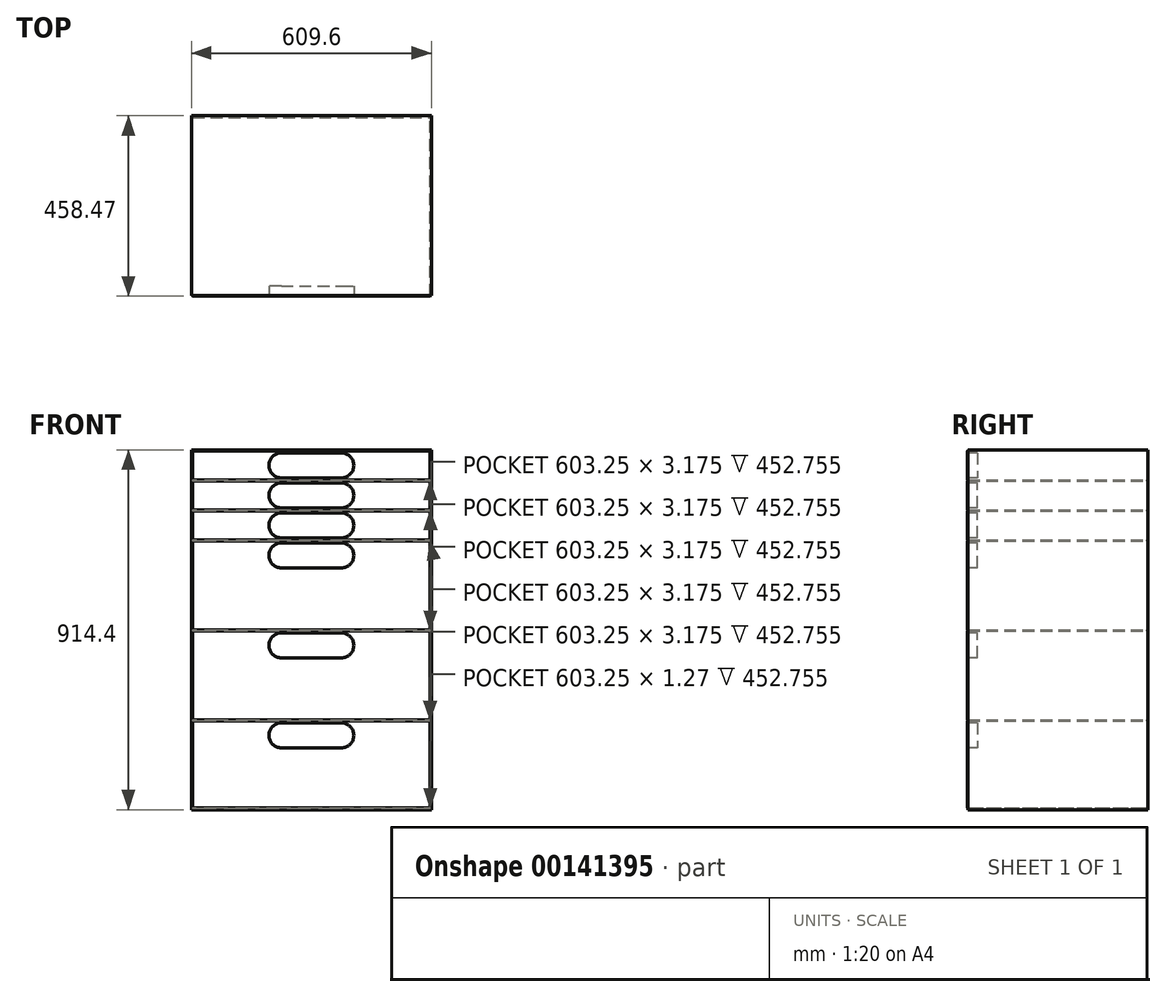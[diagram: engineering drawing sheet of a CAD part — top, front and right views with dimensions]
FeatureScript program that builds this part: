
annotation { "Feature Type Name" : "Feature", "Feature Type Description" : "" }
export const myFeature = defineFeature(function(context is Context, id is Id, definition is map)
    precondition{}
    {
        {
            var Q0;
            Q0=qCreatedBy(makeId("Top.planeOp"),FACE);
            var sketch = newSketch(context, id + "F0", { "sketchPlane" : qUnion([Q0])});
            skLineSegment(sketch, "E0.bottom", {"start": v(-304.8, 228.6) * mm, "end": v(304.8, 228.6) * mm});
            skLineSegment(sketch, "E0.top", {"start": v(-304.8, -228.6) * mm, "end": v(304.8, -228.6) * mm});
            skLineSegment(sketch, "E0.left", {"start": v(-304.8, 228.6) * mm, "end": v(-304.8, -228.6) * mm});
            skLineSegment(sketch, "E0.right", {"start": v(304.8, 228.6) * mm, "end": v(304.8, -228.6) * mm});
            skPoint(sketch, "E0.middle", {"position": v(0, 0) * mm});
            skSolve(sketch);
        }
        {
            var Q0;
            Q0 = qSketchRegion(id + "F0", true);
            extrude(context, id + "F1", {"entities" : qUnion([Q0]), "depth" : 914.4 * mm});
        }
        {
            var Q0;
            Q0=makeQuery(id+"F1.opExtrude","SWEPT_FACE",FACE,{"disambiguationData":[OSD([sQuery(id+"F0.wireOp",EDGE,"E0.top")])]});
            var sketch = newSketch(context, id + "F2", { "sketchPlane" : qUnion([Q0])});
            skPoint(sketch, "E1", {"position": v(304.8, 457.2) * mm});
            skPoint(sketch, "E2", {"position": v(0, 914.4) * mm});
            skPoint(sketch, "E3", {"position": v(0, 457.2) * mm});
            skLineSegment(sketch, "E4.bottom", {"start": v(-301.63, 911.23) * mm, "end": v(301.63, 911.23) * mm});
            skLineSegment(sketch, "E4.top", {"start": v(-301.63, 3.18) * mm, "end": v(301.63, 3.18) * mm});
            skLineSegment(sketch, "E4.left", {"start": v(-301.63, 911.23) * mm, "end": v(-301.63, 3.18) * mm});
            skLineSegment(sketch, "E4.right", {"start": v(301.63, 911.23) * mm, "end": v(301.63, 3.18) * mm});
            skSolve(sketch);
        }
        {
            var Q0;
            Q0=makeQuery(id+"F2.imprint","IMPRINT",FACE,{"disambiguationData":[TD([[makeQuery(id+"F2.imprint","IMPRINT",EDGE,{"derivedFrom":sQuery(id+"F2.wireOp",EDGE,"E4.bottom")}),-1.0]])]});
            extrude(context, id + "F3", {"entities" : qUnion([Q0]), "operationType" : NewBodyOperationType.REMOVE, "oppositeDirection" : true, "depth" : 452.75 * mm});
        }
        {
            var Q0;
            Q0=makeQuery(id+"F3.boolean.opBoolean","COPY",FACE,{"derivedFrom":makeQuery(id+"F3.opExtrude","CAP_FACE",FACE,{"disambiguationData":[OSD([sQuery(id+"F2.wireOp",EDGE,"E4.bottom"),sQuery(id+"F2.wireOp",EDGE,"E4.top"),sQuery(id+"F2.wireOp",EDGE,"E4.left"),sQuery(id+"F2.wireOp",EDGE,"E4.right")])],"isStart":false})});
            var sketch = newSketch(context, id + "F4", { "sketchPlane" : qUnion([Q0])});
            skLineSegment(sketch, "E5.bottom", {"start": v(-301.63, 911.23) * mm, "end": v(301.63, 911.23) * mm});
            skLineSegment(sketch, "E5.top", {"start": v(-301.63, 838.2) * mm, "end": v(301.63, 838.2) * mm});
            skLineSegment(sketch, "E5.left", {"start": v(-301.63, 911.23) * mm, "end": v(-301.63, 838.2) * mm});
            skLineSegment(sketch, "E5.right", {"start": v(301.63, 911.23) * mm, "end": v(301.63, 838.2) * mm});
            skLineSegment(sketch, "E6.bottom", {"start": v(-301.63, 835.02) * mm, "end": v(301.63, 835.02) * mm});
            skLineSegment(sketch, "E6.top", {"start": v(-301.63, 762) * mm, "end": v(301.63, 762) * mm});
            skLineSegment(sketch, "E6.left", {"start": v(-301.63, 835.02) * mm, "end": v(-301.63, 762) * mm});
            skLineSegment(sketch, "E6.right", {"start": v(301.63, 835.02) * mm, "end": v(301.63, 762) * mm});
            skLineSegment(sketch, "E7.bottom", {"start": v(-301.63, 758.82) * mm, "end": v(301.63, 758.82) * mm});
            skLineSegment(sketch, "E7.top", {"start": v(-301.63, 685.8) * mm, "end": v(301.63, 685.8) * mm});
            skLineSegment(sketch, "E7.left", {"start": v(-301.63, 758.82) * mm, "end": v(-301.63, 685.8) * mm});
            skLineSegment(sketch, "E7.right", {"start": v(301.63, 758.82) * mm, "end": v(301.63, 685.8) * mm});
            skLineSegment(sketch, "E8.bottom", {"start": v(-301.63, 682.62) * mm, "end": v(301.63, 682.62) * mm});
            skLineSegment(sketch, "E8.top", {"start": v(-301.63, 457.2) * mm, "end": v(301.63, 457.2) * mm});
            skLineSegment(sketch, "E8.left", {"start": v(-301.63, 682.62) * mm, "end": v(-301.63, 457.2) * mm});
            skLineSegment(sketch, "E8.right", {"start": v(301.63, 682.62) * mm, "end": v(301.63, 457.2) * mm});
            skLineSegment(sketch, "E9.bottom", {"start": v(-301.63, 454.02) * mm, "end": v(301.63, 454.02) * mm});
            skLineSegment(sketch, "E9.top", {"start": v(-301.63, 228.6) * mm, "end": v(301.63, 228.6) * mm});
            skLineSegment(sketch, "E9.left", {"start": v(-301.63, 454.02) * mm, "end": v(-301.63, 228.6) * mm});
            skLineSegment(sketch, "E9.right", {"start": v(301.63, 454.02) * mm, "end": v(301.63, 228.6) * mm});
            skLineSegment(sketch, "E10.bottom", {"start": v(-301.63, 225.42) * mm, "end": v(301.63, 225.42) * mm});
            skLineSegment(sketch, "E10.top", {"start": v(-301.63, 4.44) * mm, "end": v(301.63, 4.44) * mm});
            skLineSegment(sketch, "E10.left", {"start": v(-301.63, 225.42) * mm, "end": v(-301.63, 4.44) * mm});
            skLineSegment(sketch, "E10.right", {"start": v(301.63, 225.42) * mm, "end": v(301.63, 4.44) * mm});
            skSolve(sketch);
        }
        {
            var Q0;
            Q0 = qSketchRegion(id + "F4", true);
            extrude(context, id + "F5", {"entities" : qUnion([Q0]), "operationType" : NewBodyOperationType.ADD, "depth" : 454.02 * mm});
        }
        {
            var Q0;
            Q0=makeQuery(id+"F5.opExtrude","CAP_FACE",FACE,{"disambiguationData":[OSD([sQuery(id+"F4.wireOp",EDGE,"E5.bottom"),sQuery(id+"F4.wireOp",EDGE,"E5.top"),sQuery(id+"F4.wireOp",EDGE,"E5.left"),sQuery(id+"F4.wireOp",EDGE,"E5.right")])],"isStart":false});
            var sketch = newSketch(context, id + "F6", { "sketchPlane" : qUnion([Q0])});
            skLineSegment(sketch, "E11", {"start": v(0, 911.23) * mm, "end": v(0, 0) * mm});
            skLineSegment(sketch, "E12.bottom", {"start": v(-76.2, 906.46) * mm, "end": v(76.2, 906.46) * mm});
            skLineSegment(sketch, "E12.top", {"start": v(-76.2, 842.96) * mm, "end": v(76.2, 842.96) * mm});
            skArc(sketch, "E13", {"start": v(-76.2, 906.46) * mm, "mid": v(-107.95, 874.71) * mm, "end": v(-76.2, 842.96) * mm});
            skArc(sketch, "E14", {"start": v(76.2, 842.96) * mm, "mid": v(107.95, 874.71) * mm, "end": v(76.2, 906.46) * mm});
            skLineSegment(sketch, "E15.bottom", {"start": v(-76.2, 830.25) * mm, "end": v(76.2, 830.25) * mm});
            skLineSegment(sketch, "E15.top", {"start": v(-76.2, 766.75) * mm, "end": v(76.2, 766.75) * mm});
            skArc(sketch, "E16", {"start": v(-76.2, 830.25) * mm, "mid": v(-107.95, 798.5) * mm, "end": v(-76.2, 766.75) * mm});
            skArc(sketch, "E17", {"start": v(76.2, 766.75) * mm, "mid": v(107.95, 798.5) * mm, "end": v(76.2, 830.25) * mm});
            skLineSegment(sketch, "E18.bottom", {"start": v(-76.2, 754.05) * mm, "end": v(76.2, 754.05) * mm});
            skLineSegment(sketch, "E18.top", {"start": v(-76.2, 690.55) * mm, "end": v(76.2, 690.55) * mm});
            skArc(sketch, "E19", {"start": v(-76.2, 754.05) * mm, "mid": v(-107.95, 722.3) * mm, "end": v(-76.2, 690.55) * mm});
            skArc(sketch, "E20", {"start": v(76.2, 690.55) * mm, "mid": v(107.95, 722.3) * mm, "end": v(76.2, 754.05) * mm});
            skLineSegment(sketch, "E21.bottom", {"start": v(-76.2, 677.85) * mm, "end": v(76.2, 677.85) * mm});
            skLineSegment(sketch, "E21.top", {"start": v(-76.2, 614.35) * mm, "end": v(76.2, 614.35) * mm});
            skArc(sketch, "E22", {"start": v(-76.2, 677.85) * mm, "mid": v(-107.95, 646.1) * mm, "end": v(-76.2, 614.35) * mm});
            skArc(sketch, "E23", {"start": v(76.2, 614.35) * mm, "mid": v(107.95, 646.1) * mm, "end": v(76.2, 677.85) * mm});
            skLineSegment(sketch, "E24.bottom", {"start": v(-76.2, 449.25) * mm, "end": v(76.2, 449.25) * mm});
            skLineSegment(sketch, "E24.top", {"start": v(-76.2, 385.75) * mm, "end": v(76.2, 385.75) * mm});
            skArc(sketch, "E25", {"start": v(-76.2, 449.25) * mm, "mid": v(-107.95, 417.5) * mm, "end": v(-76.2, 385.75) * mm});
            skArc(sketch, "E26", {"start": v(76.2, 385.75) * mm, "mid": v(107.95, 417.5) * mm, "end": v(76.2, 449.25) * mm});
            skLineSegment(sketch, "E27.bottom", {"start": v(-76.2, 220.65) * mm, "end": v(76.2, 220.65) * mm});
            skLineSegment(sketch, "E27.top", {"start": v(-76.2, 157.15) * mm, "end": v(76.2, 157.15) * mm});
            skArc(sketch, "E28", {"start": v(-76.2, 220.65) * mm, "mid": v(-107.95, 188.9) * mm, "end": v(-76.2, 157.15) * mm});
            skArc(sketch, "E29", {"start": v(76.2, 157.15) * mm, "mid": v(107.95, 188.9) * mm, "end": v(76.2, 220.65) * mm});
            skSolve(sketch);
        }
        {
            var Q0;
            Q0 = qSketchRegion(id + "F6", true);
            extrude(context, id + "F7", {"entities" : qUnion([Q0]), "operationType" : NewBodyOperationType.REMOVE, "oppositeDirection" : true, "depth" : 25.4 * mm});
        }
    });
